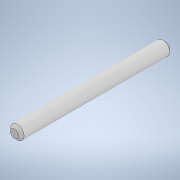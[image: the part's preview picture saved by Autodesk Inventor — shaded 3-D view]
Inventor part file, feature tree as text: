
AUTODESK INVENTOR PART (.ipt)
format: ipt  version: 2022 (Build 260153000, 153)  size: 96,768 bytes
history: native  units: mm
features: extrude x1, chamfer x1, sketch x1
ambient origin geometry x8: Origin, YZ Plane, XZ Plane, XY Plane, X Axis, Y Axis, Z Axis, Center Point
bodies: Solid1 (feature_tree)
feature tree (3):
  extrude  "Extrusion1"  Depth=55.0mm TaperAngle=0.0deg
  chamfer  "Chamfer1"  Distance=2.0mm Angle=45.0deg
  sketch  "Sketch1"  dims[d0=5.0mm d1=55.0mm d2=0.0mm d3=1.0mm d4=2.0mm d5=45.0deg]
